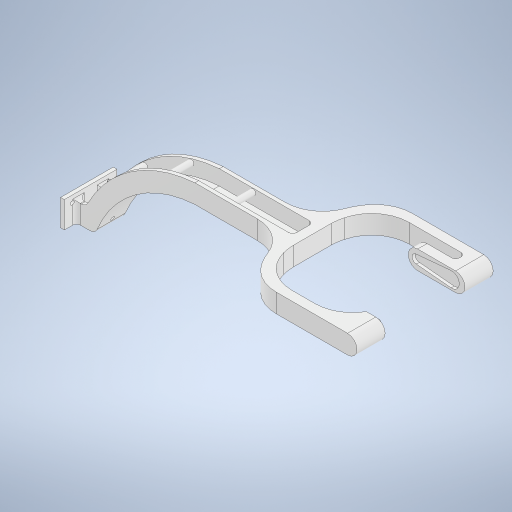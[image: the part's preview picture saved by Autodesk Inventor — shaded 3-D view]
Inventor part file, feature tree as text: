
AUTODESK INVENTOR PART (.ipt)
format: ipt  version: 2023 (Build 270158000, 158)  size: 557,056 bytes
history: native  units: mm
features: extrude x10, sketch x3, fillet x2, move_body x2, other x1, shell x1
ambient origin geometry x8: Origin, YZ Plane, XZ Plane, XY Plane, X Axis, Y Axis, Z Axis, Center Point
bodies: Volumenkörper2 (feature_tree)
feature tree (19):
  sketch  "Skizze1"  dims[d4=5.0mm d13=10.0mm]
  sketch  "Skizze2"  dims[d67=10.0mm d68=5.0mm]
  sketch  "Skizze3"  dims[d69=5.0mm d70=20.0mm d75=2.0mm d80=10.0mm d82=20.0mm d83=18.0mm d84=10.0mm d85=40.0mm d89=40.0mm d100=60.0mm d101=70.0mm d102=4.0mm d103=4.0mm d104=30.0mm d107=5.0mm d108=10.0mm d109=0.0mm d110=15.0mm d111=0.0mm d122=8.0mm d128=2.95mm d129=3.5mm d130=0.0mm d131=42.501mm d133=50.0mm d134=50.0mm d141=2.0mm d142=5.0mm d146=0.174533mm d147=2.0mm d148=0.0mm d159=2.0mm d160=10.0mm d161=0.0mm d162=75.0mm d163=0.0mm d164=1.6mm d165=0.0mm d166=10.0mm d167=0.0mm d168=20.0mm d169=2.0mm d170=2.0mm d171=2.0mm d172=3.6mm d173=3.6mm d174=3.6mm d175=2.0mm d176=0.0mm d177=2.0mm d178=3.0mm d179=3.0mm d180=15.0mm d181=0.0mm d182=3.0mm d183=3.0mm d185=60.0mm d186=30.0mm d187=30.0mm d188=5.0mm d189=30.0mm d190=5.0mm d191=30.0mm d192=65.0mm d193=190.0mm d194=178.0mm d196=180.0deg d197=10.0mm d198=0.0mm d199=-72.5mm d28=0.5mm d29=0.872665mm d30=0.5mm d31=0.872665mm d35=0.5mm d36=0.872665mm d37=0.5mm d38=0.872665mm]
  extrude  "Extrusion5"  Depth=10.0mm
  extrude  "Extrusion6"  Depth=5.0mm
  extrude  "Extrusion10"  Depth=20.0mm
  other  "Flächenverjüngung1"
  extrude  "Extrusion12"  Depth=2.0mm
  shell  "Wandung2"  Thickness=10.0mm
  extrude  "Extrusion14"  Depth=20.0mm
  extrude  "Extrusion15"  Depth=10.0mm
  extrude  "Extrusion16"  Depth=10.0mm
  extrude  "Extrusion17"  Depth=40.0mm
  fillet  "Rundung2"  Radius=40.0mm
  extrude  "Extrusion18"  Depth=60.0mm
  fillet  "Rundung3"  Radius=70.0mm
  extrude  "Extrusion19"  Depth=10.0mm
  move_body  "Move Body1"
  move_body  "Move Body2"
